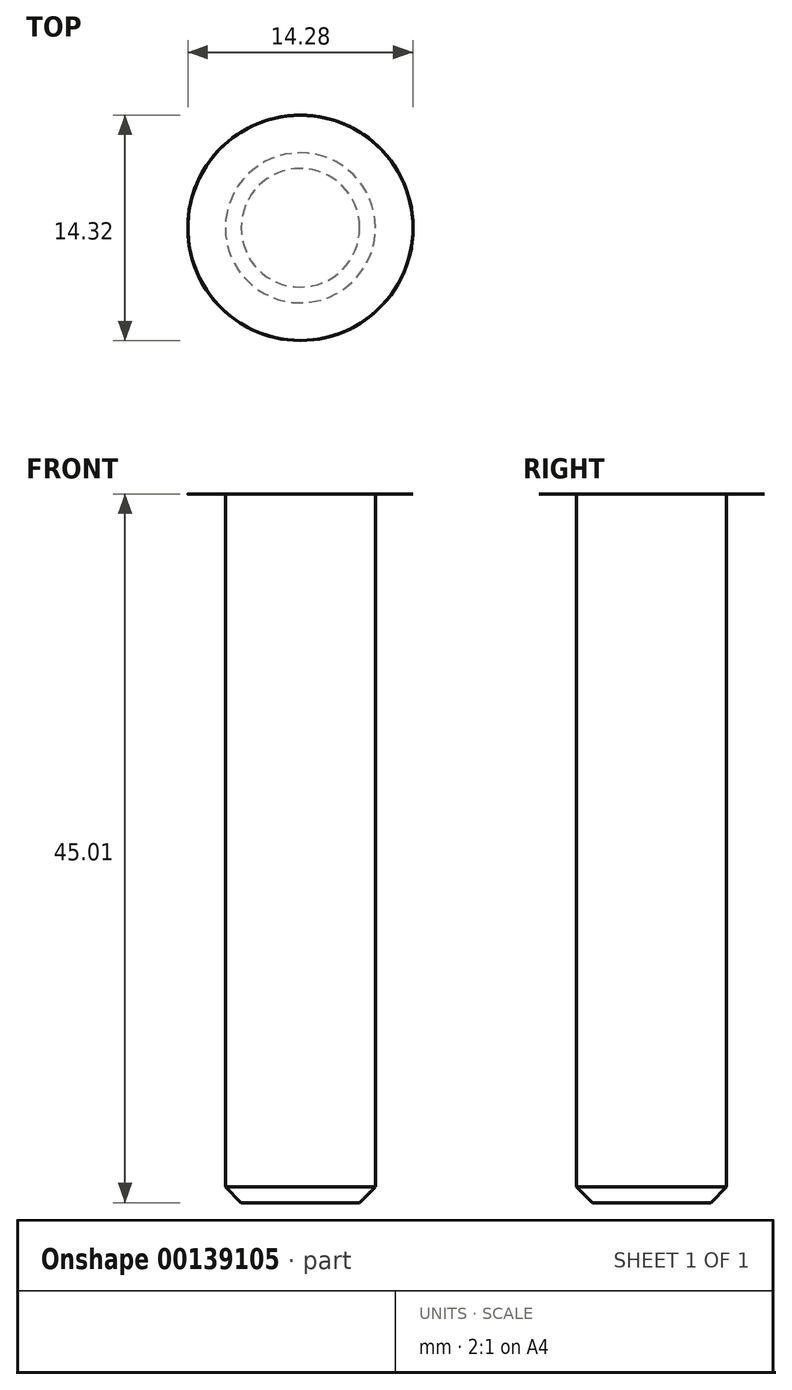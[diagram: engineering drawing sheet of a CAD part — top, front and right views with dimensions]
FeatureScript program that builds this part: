
annotation { "Feature Type Name" : "Feature", "Feature Type Description" : "" }
export const myFeature = defineFeature(function(context is Context, id is Id, definition is map)
    precondition{}
    {
        {
            var Q0;
            Q0=qCreatedBy(makeId("Top.planeOp"),FACE);
            var sketch = newSketch(context, id + "F0", { "sketchPlane" : qUnion([Q0])});
            skCircle(sketch, "E0", {"center": v(0, 0) * mm, "radius": 4.76 * mm});
            skCircle(sketch, "E1.cCircle", {"center": v(0, 0) * mm, "radius": 7.14 * mm, "construction": true});
            skLineSegment(sketch, "E1.0", {"start": v(7.14, 4.12) * mm, "end": v(7.14, -4.12) * mm});
            skLineSegment(sketch, "E1.1", {"start": v(7.14, -4.12) * mm, "end": v(0, -8.25) * mm});
            skLineSegment(sketch, "E1.2", {"start": v(0, -8.25) * mm, "end": v(-7.14, -4.12) * mm});
            skLineSegment(sketch, "E1.3", {"start": v(-7.14, -4.12) * mm, "end": v(-7.14, 4.12) * mm});
            skLineSegment(sketch, "E1.4", {"start": v(-7.14, 4.12) * mm, "end": v(0, 8.25) * mm});
            skLineSegment(sketch, "E1.5", {"start": v(0, 8.25) * mm, "end": v(7.14, 4.12) * mm});
            skPoint(sketch, "E1.0.midPoint", {"position": v(7.14, 0) * mm});
            skCircle(sketch, "E2", {"center": v(0, 0) * mm, "radius": 8.25 * mm});
            skSolve(sketch);
        }
        {
            var Q0;
            {var subQ0=sQuery(id+"F0.wireOp",EDGE,"E1.1");Q0=makeQuery(id+"F0.imprint","IMPRINT",FACE,{"disambiguationData":[TD([[makeQuery(id+"F0.imprint","IMPRINT",EDGE,{"derivedFrom":subQ0}),1.0]])]});}
            var Q1;
            {var subQ0=sQuery(id+"F0.wireOp",EDGE,"E1.0");Q1=makeQuery(id+"F0.imprint","IMPRINT",FACE,{"disambiguationData":[TD([[makeQuery(id+"F0.imprint","IMPRINT",EDGE,{"derivedFrom":subQ0}),1.0]])]});}
            var Q2;
            {var subQ0=sQuery(id+"F0.wireOp",EDGE,"E1.5");Q2=makeQuery(id+"F0.imprint","IMPRINT",FACE,{"disambiguationData":[TD([[makeQuery(id+"F0.imprint","IMPRINT",EDGE,{"derivedFrom":subQ0}),1.0]])]});}
            var Q3;
            {var subQ0=sQuery(id+"F0.wireOp",EDGE,"E1.4");Q3=makeQuery(id+"F0.imprint","IMPRINT",FACE,{"disambiguationData":[TD([[makeQuery(id+"F0.imprint","IMPRINT",EDGE,{"derivedFrom":subQ0}),1.0]])]});}
            var Q4;
            Q4=makeQuery(id+"F0.imprint","IMPRINT",FACE,{"disambiguationData":[TD([[makeQuery(id+"F0.imprint","IMPRINT",EDGE,{"derivedFrom":sQuery(id+"F0.wireOp",EDGE,"E0")}),-1.0]])]});
            var Q5;
            Q5=makeQuery(id+"F0.imprint","IMPRINT",FACE,{"disambiguationData":[TD([[makeQuery(id+"F0.imprint","IMPRINT",EDGE,{"derivedFrom":sQuery(id+"F0.wireOp",EDGE,"E0")}),1.0]])]});
            var Q6;
            {var subQ0=sQuery(id+"F0.wireOp",EDGE,"E1.3");Q6=makeQuery(id+"F0.imprint","IMPRINT",FACE,{"disambiguationData":[TD([[makeQuery(id+"F0.imprint","IMPRINT",EDGE,{"derivedFrom":subQ0}),1.0]])]});}
            var Q7;
            {var subQ0=sQuery(id+"F0.wireOp",EDGE,"E1.2");Q7=makeQuery(id+"F0.imprint","IMPRINT",FACE,{"disambiguationData":[TD([[makeQuery(id+"F0.imprint","IMPRINT",EDGE,{"derivedFrom":subQ0}),1.0]])]});}
            extrude(context, id + "F1", {"entities" : qUnion([Q0, Q1, Q2, Q3, Q4, Q5, Q6, Q7]), "depth" : 1 / 101.6 * mm});
        }
        {
            var Q0;
            Q0=makeQuery(id+"F1.opExtrude","CAP_EDGE",EDGE,{"disambiguationData":[OSD([sQuery(id+"F0.wireOp",EDGE,"E2")])],"isStart":false});
            chamfer(context, id + "F2", {"entities" : qUnion([Q0]), "width" : 1.1 * mm, "tangentPropagation" : true});
        }
        {
            var Q0;
            Q0=makeQuery(id+"F0.imprint","IMPRINT",FACE,{"disambiguationData":[TD([[makeQuery(id+"F0.imprint","IMPRINT",EDGE,{"derivedFrom":sQuery(id+"F0.wireOp",EDGE,"E0")}),-1.0]])]});
            var Q1;
            Q1=makeQuery(id+"F0.imprint","IMPRINT",FACE,{"disambiguationData":[TD([[makeQuery(id+"F0.imprint","IMPRINT",EDGE,{"derivedFrom":sQuery(id+"F0.wireOp",EDGE,"E0")}),1.0]])]});
            extrude(context, id + "F3", {"entities" : qUnion([Q0, Q1]), "operationType" : NewBodyOperationType.INTERSECT, "depth" : 1 / 101.6 * mm});
        }
        {
            var Q0;
            Q0=makeQuery(id+"F0.imprint","IMPRINT",FACE,{"disambiguationData":[TD([[makeQuery(id+"F0.imprint","IMPRINT",EDGE,{"derivedFrom":sQuery(id+"F0.wireOp",EDGE,"E0")}),1.0]])]});
            extrude(context, id + "F4", {"entities" : qUnion([Q0]), "operationType" : NewBodyOperationType.ADD, "oppositeDirection" : true, "depth" : 45 * mm});
        }
        {
            var Q0;
            Q0=makeQuery(id+"F4.opExtrude","CAP_EDGE",EDGE,{"disambiguationData":[OSD([sQuery(id+"F0.wireOp",EDGE,"E0")])],"isStart":false});
            chamfer(context, id + "F5", {"entities" : qUnion([Q0]), "width" : 1 * mm, "tangentPropagation" : true});
        }
    });
